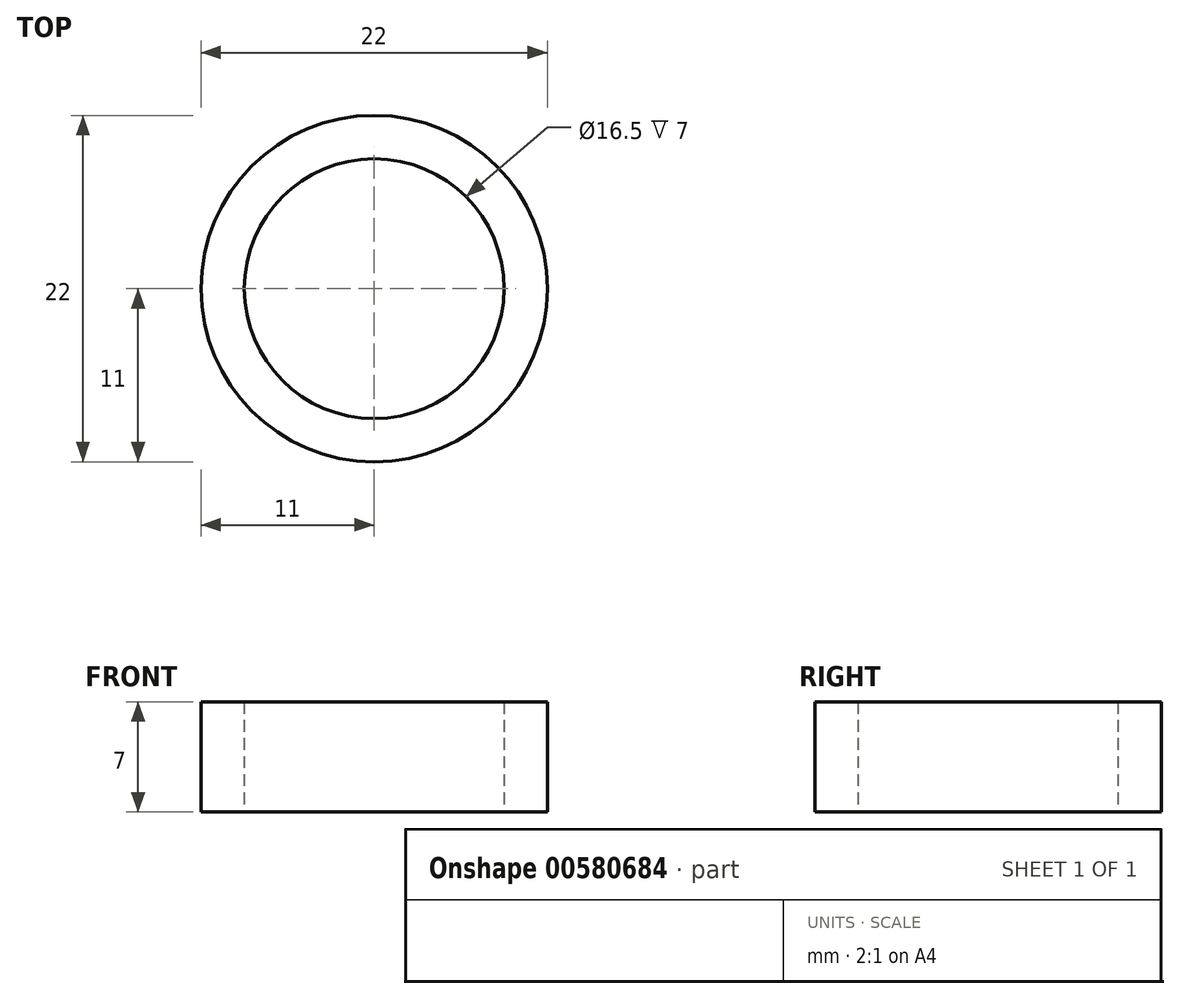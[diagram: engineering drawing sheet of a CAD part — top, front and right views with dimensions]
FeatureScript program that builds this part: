
annotation { "Feature Type Name" : "Feature", "Feature Type Description" : "" }
export const myFeature = defineFeature(function(context is Context, id is Id, definition is map)
    precondition{}
    {
        {
            var Q0;
            Q0=qCreatedBy(makeId("Top.planeOp"),FACE);
            var sketch = newSketch(context, id + "F0", { "sketchPlane" : qUnion([Q0])});
            skCircle(sketch, "E0", {"center": v(0, 0) * mm, "radius": 8.25 * mm});
            skCircle(sketch, "E1", {"center": v(0, 0) * mm, "radius": 11 * mm});
            skSolve(sketch);
        }
        {
            var Q0;
            Q0=makeQuery(id+"F0.imprint","IMPRINT",FACE,{"disambiguationData":[TD([[makeQuery(id+"F0.imprint","IMPRINT",EDGE,{"derivedFrom":sQuery(id+"F0.wireOp",EDGE,"E0")}),-1.0]])]});
            extrude(context, id + "F1", {"entities" : qUnion([Q0]), "depth" : 7 * mm});
        }
    });
